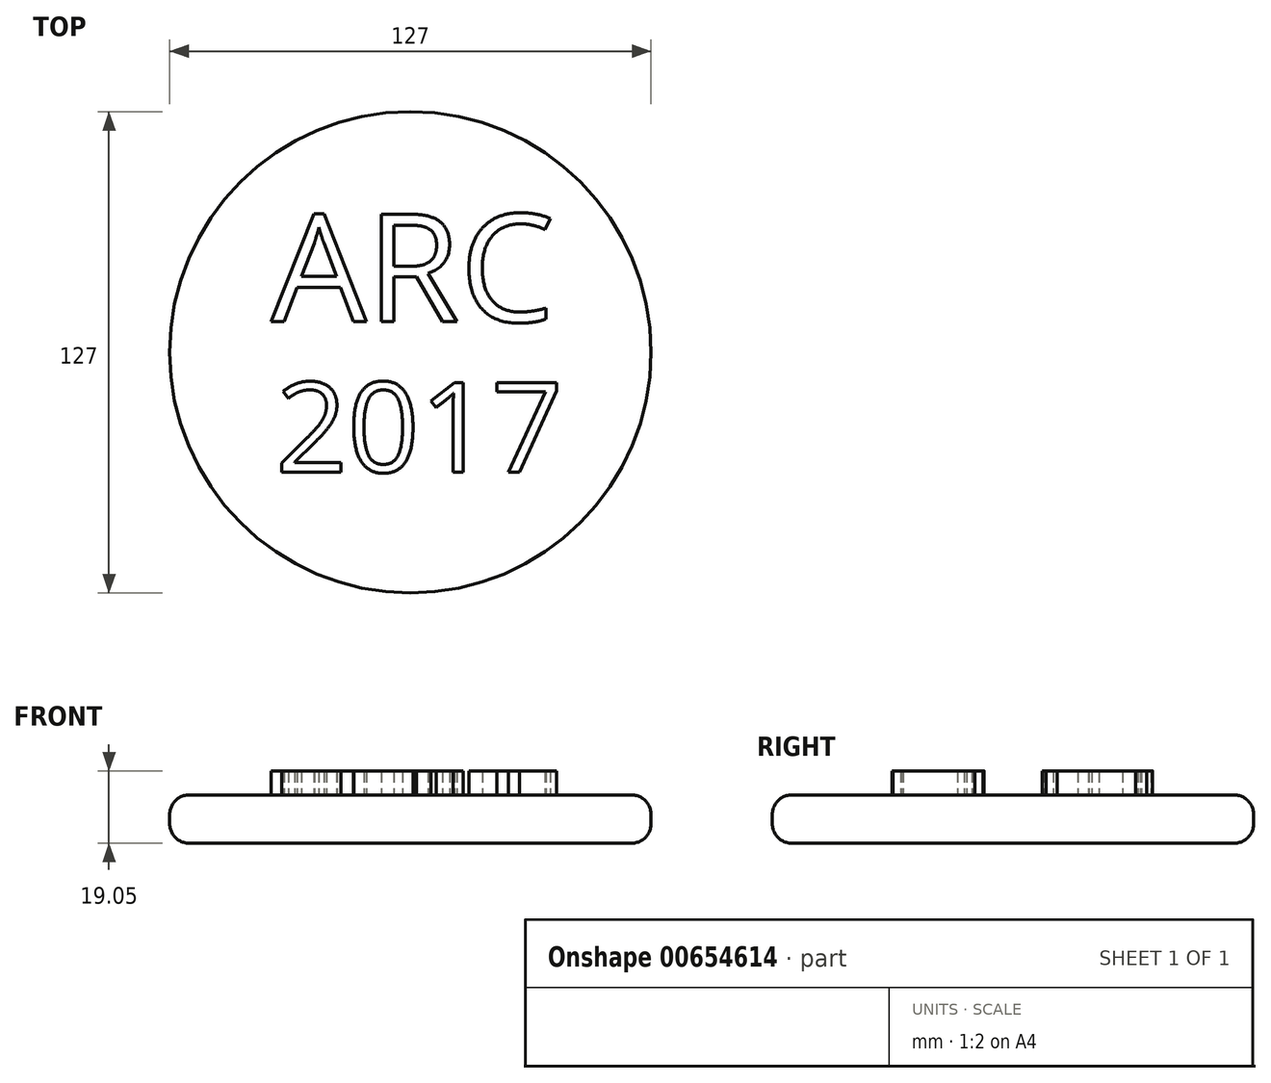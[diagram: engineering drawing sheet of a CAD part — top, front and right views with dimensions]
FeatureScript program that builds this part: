
annotation { "Feature Type Name" : "Feature", "Feature Type Description" : "" }
export const myFeature = defineFeature(function(context is Context, id is Id, definition is map)
    precondition{}
    {
        {
            var Q0;
            Q0=qCreatedBy(makeId("Top.planeOp"),FACE);
            var sketch = newSketch(context, id + "F0", { "sketchPlane" : qUnion([Q0])});
            skCircle(sketch, "E0", {"center": v(0, 0) * mm, "radius": 63.5 * mm});
            skSolve(sketch);
        }
        {
            var Q0;
            Q0=makeQuery(id+"F0.imprint","IMPRINT",FACE,{"disambiguationData":[TD([[makeQuery(id+"F0.imprint","IMPRINT",EDGE,{"derivedFrom":sQuery(id+"F0.wireOp",EDGE,"E0")}),1.0]])]});
            extrude(context, id + "F1", {"entities" : qUnion([Q0]), "depth" : 12.7 * mm, "offsetDistance" : 25.4 * mm});
        }
        {
            var Q0;
            Q0=makeQuery(id+"F1.opExtrude","CAP_FACE",FACE,{"disambiguationData":[OSD([sQuery(id+"F0.wireOp",EDGE,"E0")])],"isStart":false});
            var sketch = newSketch(context, id + "F2", { "sketchPlane" : qUnion([Q0])});
            skText(sketch, "E1", { "text": "ARC", "fontName": "OpenSans-Regular.ttf"});
            const initialGuessF2  = {"E1": [-0.0367, 0.00808, 1, 0, 0.02862]};
            skSetInitialGuess(sketch, initialGuessF2);
            skSolve(sketch);
        }
        {
            var Q0;
            Q0 = qSketchRegion(id + "F2", true);
            extrude(context, id + "F3", {"entities" : qUnion([Q0]), "operationType" : NewBodyOperationType.ADD, "depth" : 6.35 * mm, "offsetDistance" : 25.4 * mm});
        }
        {
            var Q0;
            {var subQ0=sQuery(id+"F0.wireOp",EDGE,"E0");Q0=makeQuery(id+"F3.boolean.opBoolean","SPLIT",FACE,{"disambiguationData":[TD([makeQuery(id+"F1.opExtrude","SWEPT_FACE",FACE,{"disambiguationData":[OSD([subQ0])]})])],"derivedFrom":makeQuery(id+"F1.opExtrude","CAP_FACE",FACE,{"disambiguationData":[OSD([subQ0])],"isStart":false})});}
            var sketch = newSketch(context, id + "F4", { "sketchPlane" : qUnion([Q0])});
            skText(sketch, "E2", { "text": "2017", "fontName": "OpenSans-Regular.ttf"});
            const initialGuessF4  = {"E2": [-0.03552, -0.0316, 1, 0, 0.02384]};
            skSetInitialGuess(sketch, initialGuessF4);
            skSolve(sketch);
        }
        {
            var Q0;
            Q0 = qSketchRegion(id + "F4", true);
            extrude(context, id + "F5", {"entities" : qUnion([Q0]), "operationType" : NewBodyOperationType.ADD, "depth" : 6.35 * mm, "offsetDistance" : 25.4 * mm});
        }
        {
            var Q0;
            Q0=makeQuery(id+"F1.opExtrude","SWEPT_FACE",FACE,{"disambiguationData":[OSD([sQuery(id+"F0.wireOp",EDGE,"E0")])]});
            fillet(context, id + "F6", {"entities" : qUnion([Q0]), "radius" : 5.08 * mm, "tangentPropagation" : true, "allowEdgeOverflow" : false});
        }
    });
